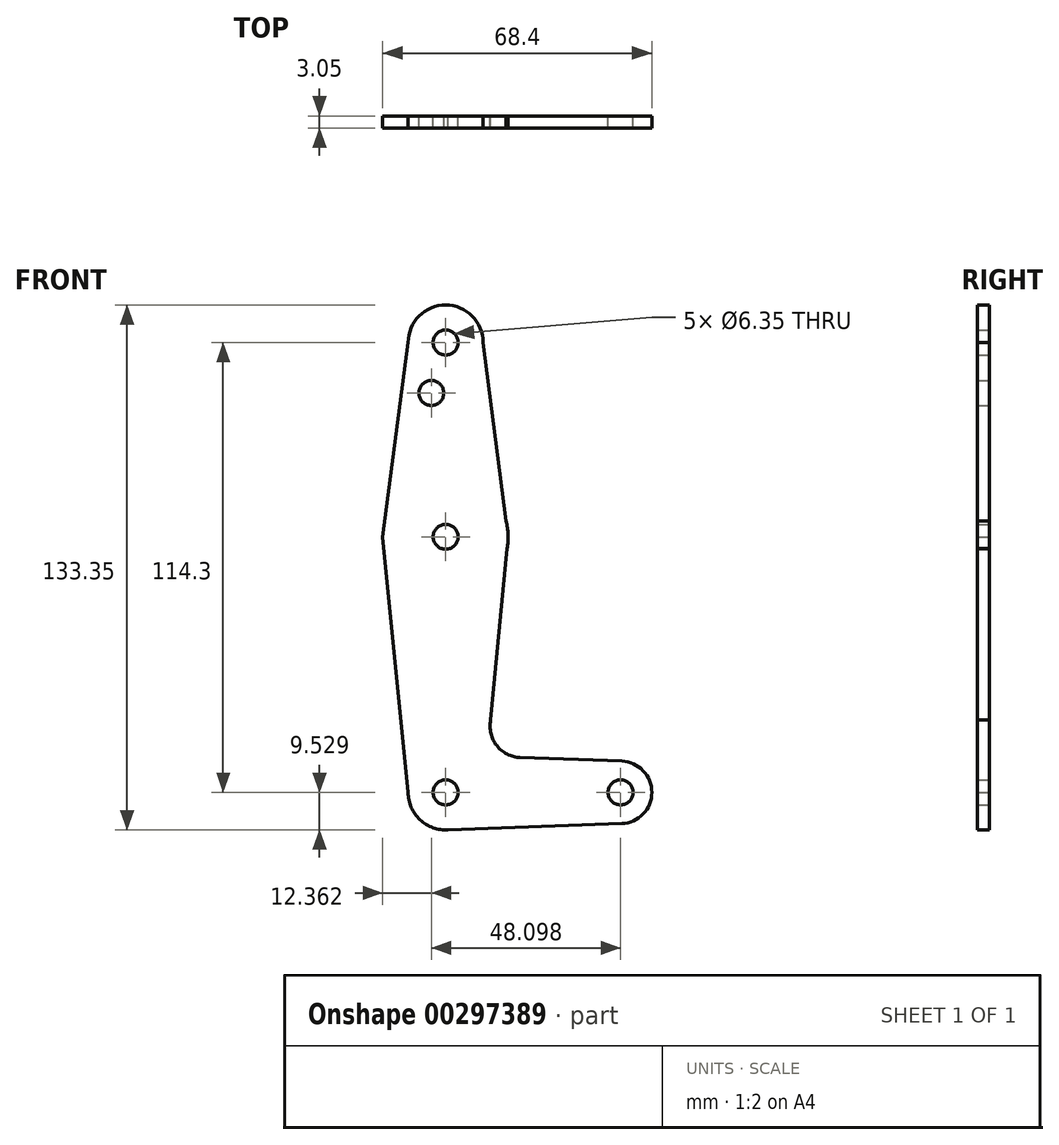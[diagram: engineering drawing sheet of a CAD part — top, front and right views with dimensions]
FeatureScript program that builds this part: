
annotation { "Feature Type Name" : "Feature", "Feature Type Description" : "" }
export const myFeature = defineFeature(function(context is Context, id is Id, definition is map)
    precondition{}
    {
        {
            var Q0;
            Q0=qCreatedBy(makeId("Front.planeOp"),FACE);
            var sketch = newSketch(context, id + "F0", { "sketchPlane" : qUnion([Q0])});
            skCircle(sketch, "E0", {"center": v(-27.9, 88.73) * mm, "radius": 9.52 * mm});
            skCircle(sketch, "E1", {"center": v(-27.9, -25.57) * mm, "radius": 9.52 * mm});
            skCircle(sketch, "E2", {"center": v(16.56, -25.57) * mm, "radius": 7.94 * mm});
            skLineSegment(sketch, "E3", {"start": v(-8.95, -16.72) * mm, "end": v(16.84, -17.64) * mm});
            skLineSegment(sketch, "E4", {"start": v(-27.85, -35.1) * mm, "end": v(16.84, -33.5) * mm});
            skCircle(sketch, "E5", {"center": v(-27.9, 88.73) * mm, "radius": 3.18 * mm});
            skCircle(sketch, "E6", {"center": v(-27.9, -25.57) * mm, "radius": 3.18 * mm});
            skCircle(sketch, "E7", {"center": v(16.56, -25.57) * mm, "radius": 3.18 * mm});
            skCircle(sketch, "E8", {"center": v(-31.54, 75.9) * mm, "radius": 3.18 * mm});
            skArc(sketch, "E9.filletArc", {"start": v(-16.45, -7.18) * mm, "mid": v(-14.9, -13.7) * mm, "end": v(-8.95, -16.72) * mm});
            skCircle(sketch, "E10", {"center": v(-27.9, 39.38) * mm, "radius": 15.88 * mm});
            skLineSegment(sketch, "E11", {"start": v(-37.42, 88.73) * mm, "end": v(-43.9, 39.38) * mm});
            skLineSegment(sketch, "E12", {"start": v(-18.37, 88.73) * mm, "end": v(-12.02, 39.38) * mm});
            skLineSegment(sketch, "E13", {"start": v(-12.02, 39.38) * mm, "end": v(-16.45, -7.18) * mm});
            skLineSegment(sketch, "E14", {"start": v(-43.9, 39.38) * mm, "end": v(-37.42, -25.57) * mm});
            skCircle(sketch, "E15", {"center": v(-27.9, 39.38) * mm, "radius": 3.18 * mm});
            skSolve(sketch);
        }
        {
            var Q0;
            Q0 = qSketchRegion(id + "F0", true);
            extrude(context, id + "F1", {"entities" : qUnion([Q0]), "depth" : 3.05 * mm});
        }
    });
